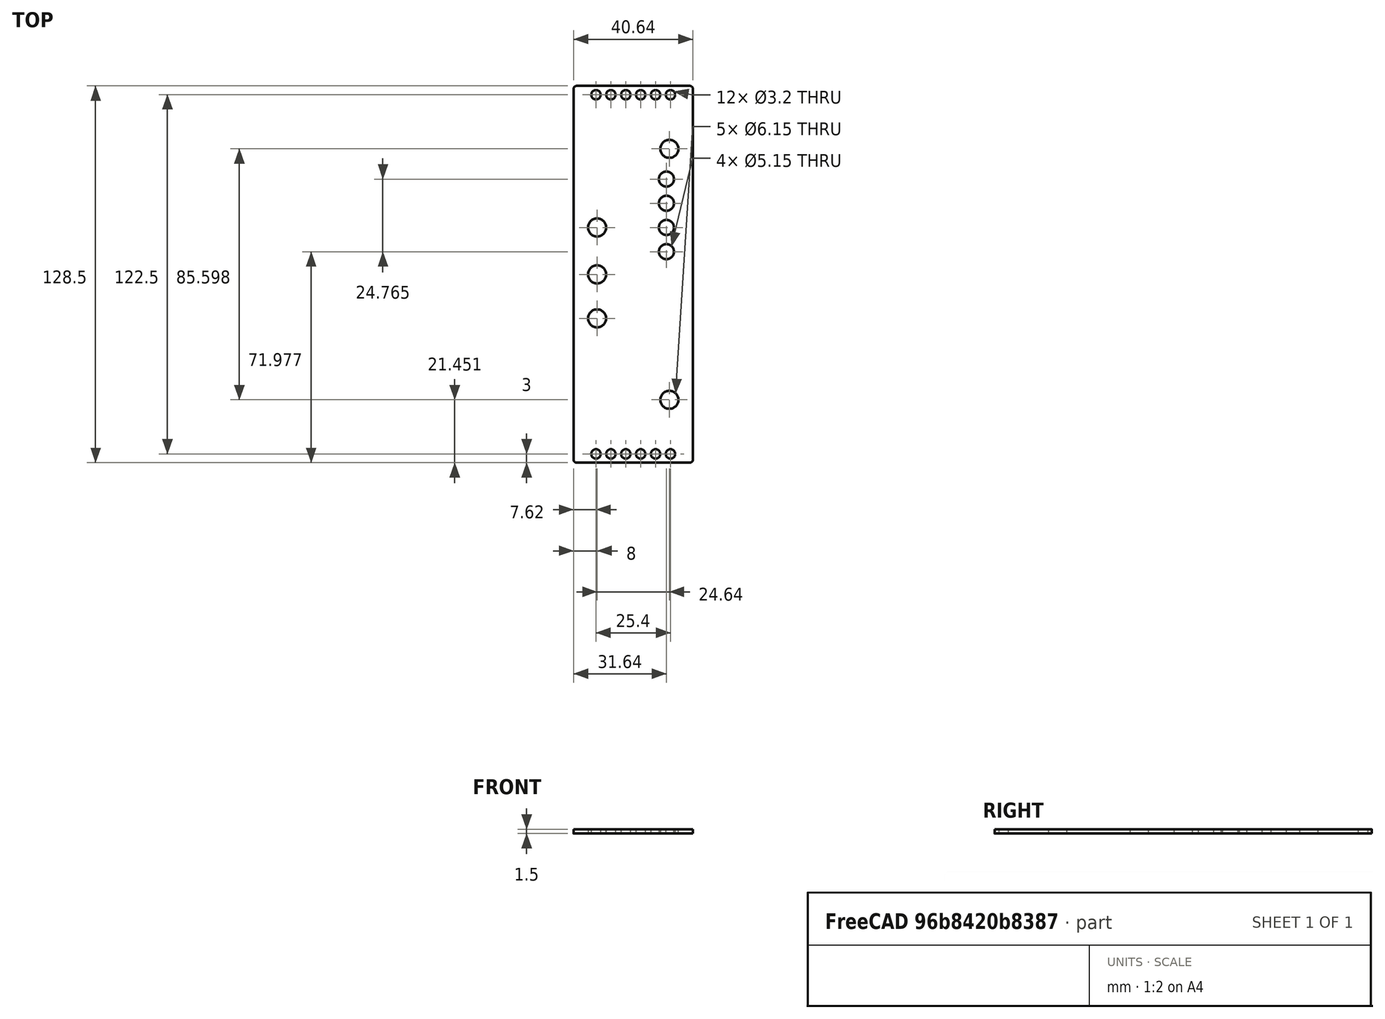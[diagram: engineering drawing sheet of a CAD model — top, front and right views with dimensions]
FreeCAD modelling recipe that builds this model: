
FCSTD DOCUMENT  (FreeCAD 0.19R24415 (Git))
Label: BitBugPanel
License: All rights reserved
LicenseURL: http://en.wikipedia.org/wiki/All_rights_reserved
objects: Sketcher::SketchObject×1, PartDesign::Pad×1, PartDesign::Fillet×1, PartDesign::Body×1, Mesh::Feature×1
note: 6 computed .brp shape members not serialized (recipe doc carries the construction recipe); baked Part::Feature solids carry a one-line shape summary decoded from their .brp

FEATURE [Sketcher::SketchObject] Sketch
  FullyConstrained = true
  MapMode = 5
  Support = -> [XY_Plane]
  expr: Constraints[72] = (128.5 - 85.598) / 2
  expr: Constraints[69] = 16 / 2
  expr: Constraints[21] = 5.08mm * 3 / 2
  sketch-geometry (25):
    g0: LineSegment StartX=-32.64 StartY=128.5 StartZ=0 EndX=8 EndY=128.5 EndZ=0
    g1: LineSegment StartX=8 StartY=128.5 StartZ=0 EndX=8 EndY=0 EndZ=0
    g2: LineSegment StartX=8 StartY=0 StartZ=0 EndX=-32.64 EndY=0 EndZ=0
    g3: LineSegment StartX=-32.64 StartY=0 StartZ=0 EndX=-32.64 EndY=128.5 EndZ=0
    g4: Circle CenterX=-25.02 CenterY=125.5 CenterZ=0 NormalX=0 NormalY=0 NormalZ=1 AngleXU=0 Radius=1.6
    g5: Circle CenterX=-19.94 CenterY=125.5 CenterZ=0 NormalX=0 NormalY=0 NormalZ=1 AngleXU=0 Radius=1.6
    g6: Circle CenterX=-25.02 CenterY=3 CenterZ=0 NormalX=0 NormalY=0 NormalZ=1 AngleXU=0 Radius=1.6
    g7: Circle CenterX=-19.94 CenterY=3 CenterZ=0 NormalX=0 NormalY=0 NormalZ=1 AngleXU=0 Radius=1.6
    g8: Circle CenterX=-14.86 CenterY=125.5 CenterZ=0 NormalX=0 NormalY=0 NormalZ=1 AngleXU=0 Radius=1.6
    g9: Circle CenterX=-9.78 CenterY=125.5 CenterZ=0 NormalX=0 NormalY=0 NormalZ=1 AngleXU=0 Radius=1.6
    g10: Circle CenterX=-4.7 CenterY=125.5 CenterZ=0 NormalX=0 NormalY=0 NormalZ=1 AngleXU=0 Radius=1.6
    g11: Circle CenterX=0.38 CenterY=125.5 CenterZ=0 NormalX=0 NormalY=0 NormalZ=1 AngleXU=0 Radius=1.6
    g12: Circle CenterX=-14.86 CenterY=3 CenterZ=0 NormalX=0 NormalY=0 NormalZ=1 AngleXU=0 Radius=1.6
    g13: Circle CenterX=-9.78 CenterY=3 CenterZ=0 NormalX=0 NormalY=0 NormalZ=1 AngleXU=0 Radius=1.6
    g14: Circle CenterX=-4.7 CenterY=3 CenterZ=0 NormalX=0 NormalY=0 NormalZ=1 AngleXU=0 Radius=1.6
    g15: Circle CenterX=0.38 CenterY=3 CenterZ=0 NormalX=0 NormalY=0 NormalZ=1 AngleXU=0 Radius=1.6
    g16: Circle CenterX=-1 CenterY=96.742 CenterZ=0 NormalX=0 NormalY=0 NormalZ=1 AngleXU=0 Radius=2.575
    g17: Circle CenterX=0 CenterY=107.049 CenterZ=0 NormalX=0 NormalY=0 NormalZ=1 AngleXU=0 Radius=3.075
    g18: Circle CenterX=0 CenterY=21.451 CenterZ=0 NormalX=0 NormalY=0 NormalZ=1 AngleXU=0 Radius=3.075
    g19: Circle CenterX=-1 CenterY=88.487 CenterZ=0 NormalX=0 NormalY=0 NormalZ=1 AngleXU=0 Radius=2.575
    g20: Circle CenterX=-1 CenterY=80.232 CenterZ=0 NormalX=0 NormalY=0 NormalZ=1 AngleXU=0 Radius=2.575
    g21: Circle CenterX=-1 CenterY=71.977 CenterZ=0 NormalX=0 NormalY=0 NormalZ=1 AngleXU=0 Radius=2.575
    g22: Circle CenterX=-24.64 CenterY=80.232 CenterZ=0 NormalX=0 NormalY=0 NormalZ=1 AngleXU=0 Radius=3.075
    g23: Circle CenterX=-24.64 CenterY=64.232 CenterZ=0 NormalX=0 NormalY=0 NormalZ=1 AngleXU=0 Radius=3.075
    g24: Circle CenterX=-24.64 CenterY=49.232 CenterZ=0 NormalX=0 NormalY=0 NormalZ=1 AngleXU=0 Radius=3.075
  constraints (75):
    c: Coincident(g0,g1)
    c: Coincident(g1,g2)
    c: Coincident(g2,g3)
    c: Coincident(g3,g0)
    c: Horizontal(g0)
    c: Horizontal(g2)
    c: Vertical(g1)
    c: Vertical(g3)
    c: Distance(g0) = 40.64
    c: Distance(g3) = 128.5
    c: DistanceX(g4,g5) = 5.08
    c: Diameter(g5) = 3.2
    c: Diameter(g4) = 3.2
    c: Diameter(g7) = 3.2
    c: Diameter(g6) = 3.2
    c: Horizontal(g6,g7)
    c: Horizontal(g4,g5)
    c: Vertical(g4,g6)
    c: Vertical(g7,g5)
    c: DistanceY(g6,g4) = 122.5
    c: DistanceY(g2,g6) = 3
    c: DistanceX(g0,g4) = 7.62
    c: Equal(g5,g8) = 3.2
    c: Horizontal(g5,g8)
    c: Horizontal(g8,g9)
    c: Horizontal(g9,g10)
    c: Horizontal(g10,g11)
    c: Distance(g5,g8) = 5.08
    c: Distance(g8,g9) = 5.08
    c: Distance(g9,g10) = 5.08
    c: Distance(g11,g10) = 5.08
    c: Equal(g7,g13) = 3.2
    c: Equal(g6,g12) = 3.2
    c: Horizontal(g12,g13)
    c: Horizontal(g14,g15)
    c: Horizontal(g7,g12)
    c: Horizontal(g13,g14)
    c: Vertical(g11,g15)
    c: Vertical(g14,g10)
    c: Vertical(g9,g13)
    c: Vertical(g12,g8)
    c: Diameter(g15) = 3.2
    c: Diameter(g14) = 3.2
    c: Diameter(g11) = 3.2
    c: Diameter(g10) = 3.2
    c: Diameter(g9) = 3.2
    c: PointOnObject(g17,g-2)
    c: PointOnObject(g18,g-2)
    c: Vertical(g21,g20)
    c: Vertical(g19,g20)
    c: Vertical(g16,g19)
    c: Vertical(g22,g23)
    c: Vertical(g24,g23)
    c: Diameter(g16) = 5.15
    c: Diameter(g19) = 5.15
    c: Diameter(g20) = 5.15
    c: Diameter(g21) = 5.15
    c: Diameter(g22) = 6.15
    c: Diameter(g23) = 6.15
    c: Diameter(g24) = 6.15
    c: Diameter(g17) = 6.15
    c: Diameter(g18) = 6.15
    c: Distance(g18,g17) = 85.598
    c: DistanceY(g16,g17) = 10.307
    c: Distance(g19,g16) = 8.255
    c: Distance(g19,g20) = 8.255
    c: Distance(g21,g20) = 8.255
    c: DistanceX(g16,g17) = 1
    c: DistanceX(g17,g0) = 8
    c: DistanceX(g0,g22) = 8
    c: Distance(g23,g22) = 16
    c: Distance(g23,g24) = 15
    c: DistanceY(g1,g18) = 21.451
    c: PointOnObject(g1,g-1)
    c: Horizontal(g22,g20)
FEATURE [PartDesign::Pad] Pad
  Direction = (1,1,1)
  Length = 1.5
  Length2 = 100
  Profile = -> Sketch
  Type = 0
FEATURE [PartDesign::Fillet] Fillet
  Base = -> Pad [Edge5,Edge8,Edge2,Edge1]
  BaseFeature = -> Pad
  Radius = 1
  SupportTransform = false
FEATURE [PartDesign::Body] Body
  Group = -> [Sketch,Pad,Fillet]
  Origin = -> Origin
  Tip = -> Fillet
FEATURE [Mesh::Feature] Mesh  label="BitBugPanel"
